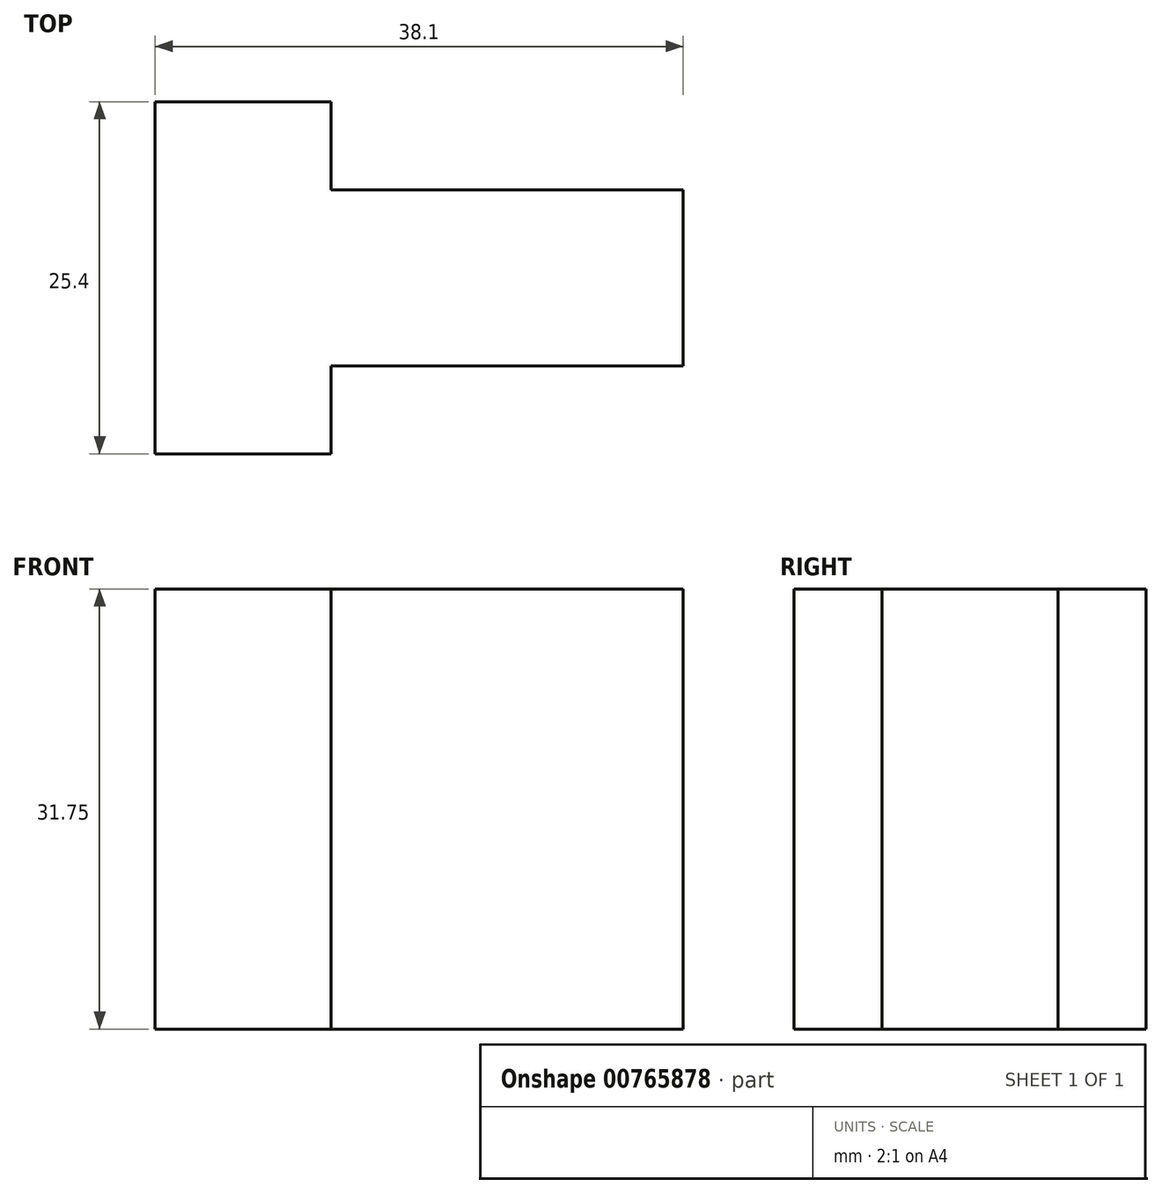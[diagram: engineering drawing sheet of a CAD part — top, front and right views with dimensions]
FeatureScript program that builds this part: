
annotation { "Feature Type Name" : "Feature", "Feature Type Description" : "" }
export const myFeature = defineFeature(function(context is Context, id is Id, definition is map)
    precondition{}
    {
        {
            var Q0;
            Q0=qCreatedBy(makeId("Top.planeOp"),FACE);
            var sketch = newSketch(context, id + "F0", { "sketchPlane" : qUnion([Q0])});
            skLineSegment(sketch, "E0", {"start": v(0, 0) * mm, "end": v(25.4, 0) * mm});
            skLineSegment(sketch, "E1", {"start": v(25.4, 0) * mm, "end": v(25.4, 12.7) * mm});
            skLineSegment(sketch, "E2", {"start": v(25.4, 12.7) * mm, "end": v(0, 12.7) * mm});
            skLineSegment(sketch, "E3", {"start": v(0, 12.7) * mm, "end": v(0, 19.05) * mm});
            skLineSegment(sketch, "E4", {"start": v(0, 19.05) * mm, "end": v(-12.7, 19.05) * mm});
            skLineSegment(sketch, "E5", {"start": v(-12.7, 19.05) * mm, "end": v(-12.7, -6.35) * mm});
            skLineSegment(sketch, "E6", {"start": v(-12.7, -6.35) * mm, "end": v(0, -6.35) * mm});
            skLineSegment(sketch, "E7", {"start": v(0, -6.35) * mm, "end": v(0, 0) * mm});
            skSolve(sketch);
        }
        {
            var Q0;
            Q0 = qSketchRegion(id + "F0", true);
            extrude(context, id + "F1", {"entities" : qUnion([Q0]), "depth" : 31.75 * mm, "offsetDistance" : 25.4 * mm});
        }
    });
